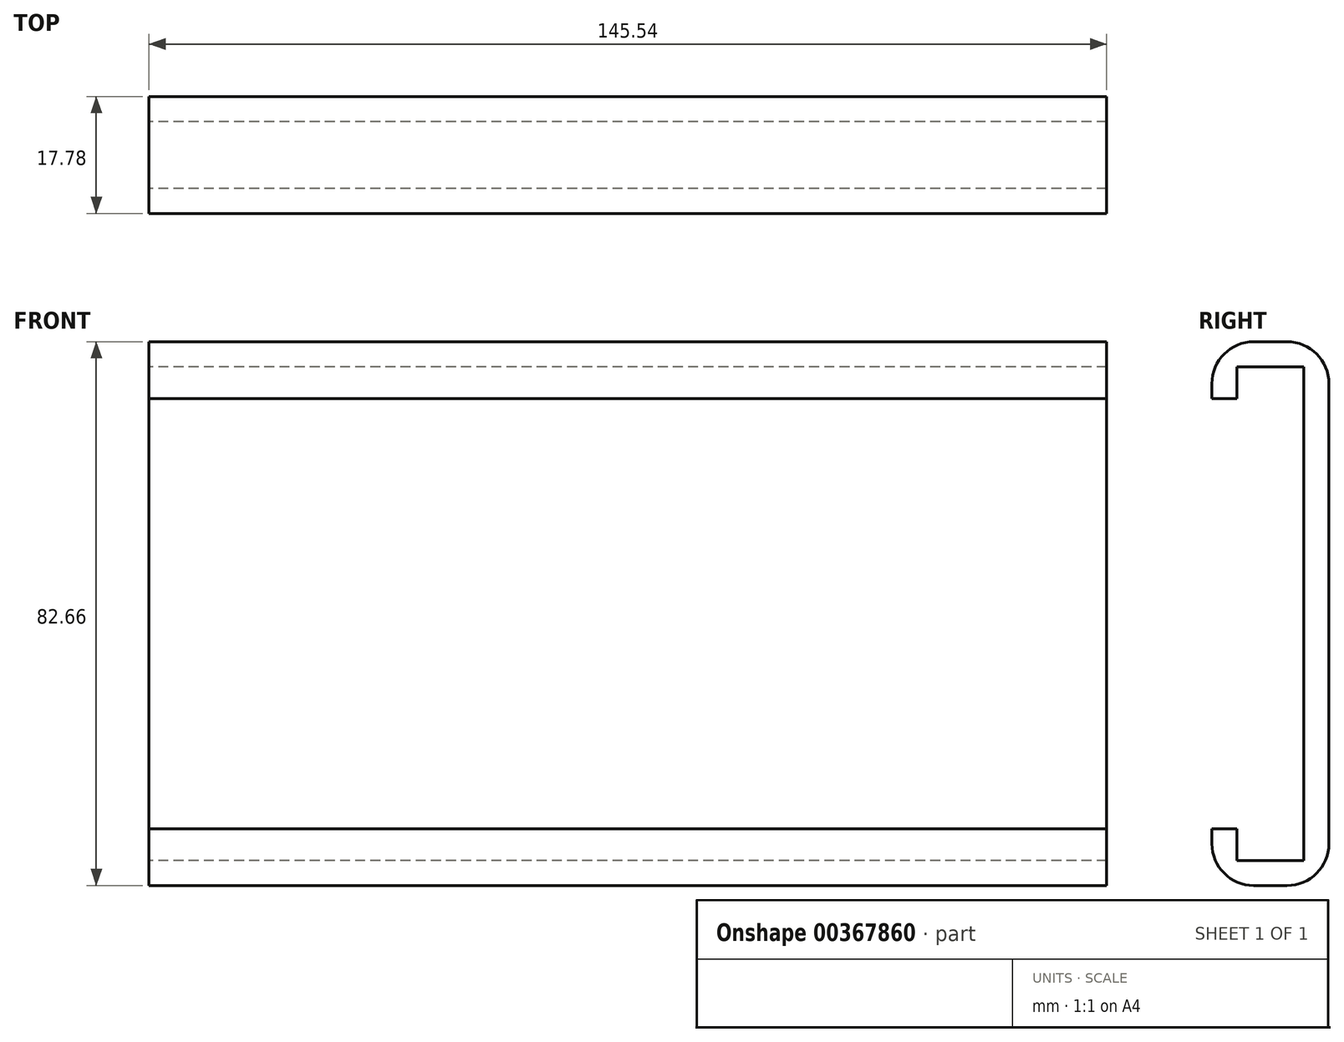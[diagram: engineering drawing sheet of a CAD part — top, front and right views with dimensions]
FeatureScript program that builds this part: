
annotation { "Feature Type Name" : "Feature", "Feature Type Description" : "" }
export const myFeature = defineFeature(function(context is Context, id is Id, definition is map)
    precondition{}
    {
        {
            var Q0;
            Q0=qCreatedBy(makeId("Right.planeOp"),FACE);
            var sketch = newSketch(context, id + "F0", { "sketchPlane" : qUnion([Q0])});
            skLineSegment(sketch, "E0", {"start": v(-8, 0) * mm, "end": v(-8, 37.52) * mm});
            skLineSegment(sketch, "E1", {"start": v(-8, 37.52) * mm, "end": v(-18.17, 37.52) * mm});
            skLineSegment(sketch, "E2", {"start": v(-18.17, 37.52) * mm, "end": v(-18.17, 32.7) * mm});
            skLineSegment(sketch, "E3", {"start": v(-18.17, 32.7) * mm, "end": v(-21.98, 32.7) * mm});
            skLineSegment(sketch, "E4", {"start": v(-21.98, 32.7) * mm, "end": v(-21.98, 34.98) * mm});
            skLineSegment(sketch, "E5", {"start": v(-15.63, 41.33) * mm, "end": v(-10.55, 41.33) * mm});
            skLineSegment(sketch, "E6", {"start": v(-4.2, 34.98) * mm, "end": v(-4.2, 0) * mm});
            skPoint(sketch, "E7.visualSharp", {"position": v(-21.98, 41.33) * mm});
            skArc(sketch, "E7.filletArc", {"start": v(-15.63, 41.33) * mm, "mid": v(-20.12, 39.47) * mm, "end": v(-21.98, 34.98) * mm});
            skPoint(sketch, "E8.visualSharp", {"position": v(-4.2, 41.33) * mm});
            skArc(sketch, "E8.filletArc", {"start": v(-4.2, 34.98) * mm, "mid": v(-6.06, 39.47) * mm, "end": v(-10.55, 41.33) * mm});
            skLineSegment(sketch, "E9.MirrorCS", {"start": v(-18.17, -37.52) * mm, "end": v(-18.17, -32.7) * mm});
            skLineSegment(sketch, "E10.MirrorCS", {"start": v(-21.98, -32.7) * mm, "end": v(-21.98, -34.98) * mm});
            skLineSegment(sketch, "E11.MirrorCS", {"start": v(-8, -37.52) * mm, "end": v(-18.17, -37.52) * mm});
            skPoint(sketch, "E12.MirrorP", {"position": v(-4.2, -41.33) * mm});
            skArc(sketch, "E13.MirrorCS", {"start": v(-15.63, -41.33) * mm, "mid": v(-20.12, -39.47) * mm, "end": v(-21.98, -34.98) * mm});
            skLineSegment(sketch, "E14.MirrorCS", {"start": v(-18.17, -32.7) * mm, "end": v(-21.98, -32.7) * mm});
            skArc(sketch, "E15.MirrorCS", {"start": v(-4.2, -34.98) * mm, "mid": v(-6.06, -39.47) * mm, "end": v(-10.55, -41.33) * mm});
            skPoint(sketch, "E16.MirrorP", {"position": v(-21.98, -41.33) * mm});
            skLineSegment(sketch, "E17.MirrorCS", {"start": v(-15.63, -41.33) * mm, "end": v(-10.55, -41.33) * mm});
            skLineSegment(sketch, "E18.MirrorCS", {"start": v(-8, 0) * mm, "end": v(-8, -37.52) * mm});
            skLineSegment(sketch, "E19.MirrorCS", {"start": v(-4.2, -34.98) * mm, "end": v(-4.2, 0) * mm});
            skSolve(sketch);
        }
        {
            var Q0;
            Q0=makeQuery(id+"F0.imprint","IMPRINT",FACE,{"disambiguationData":[TD([[makeQuery(id+"F0.imprint","IMPRINT",EDGE,{"derivedFrom":sQuery(id+"F0.wireOp",EDGE,"E0")}),-1.0]])]});
            extrude(context, id + "F1", {"entities" : qUnion([Q0]), "depth" : 145.54 * mm});
        }
    });
